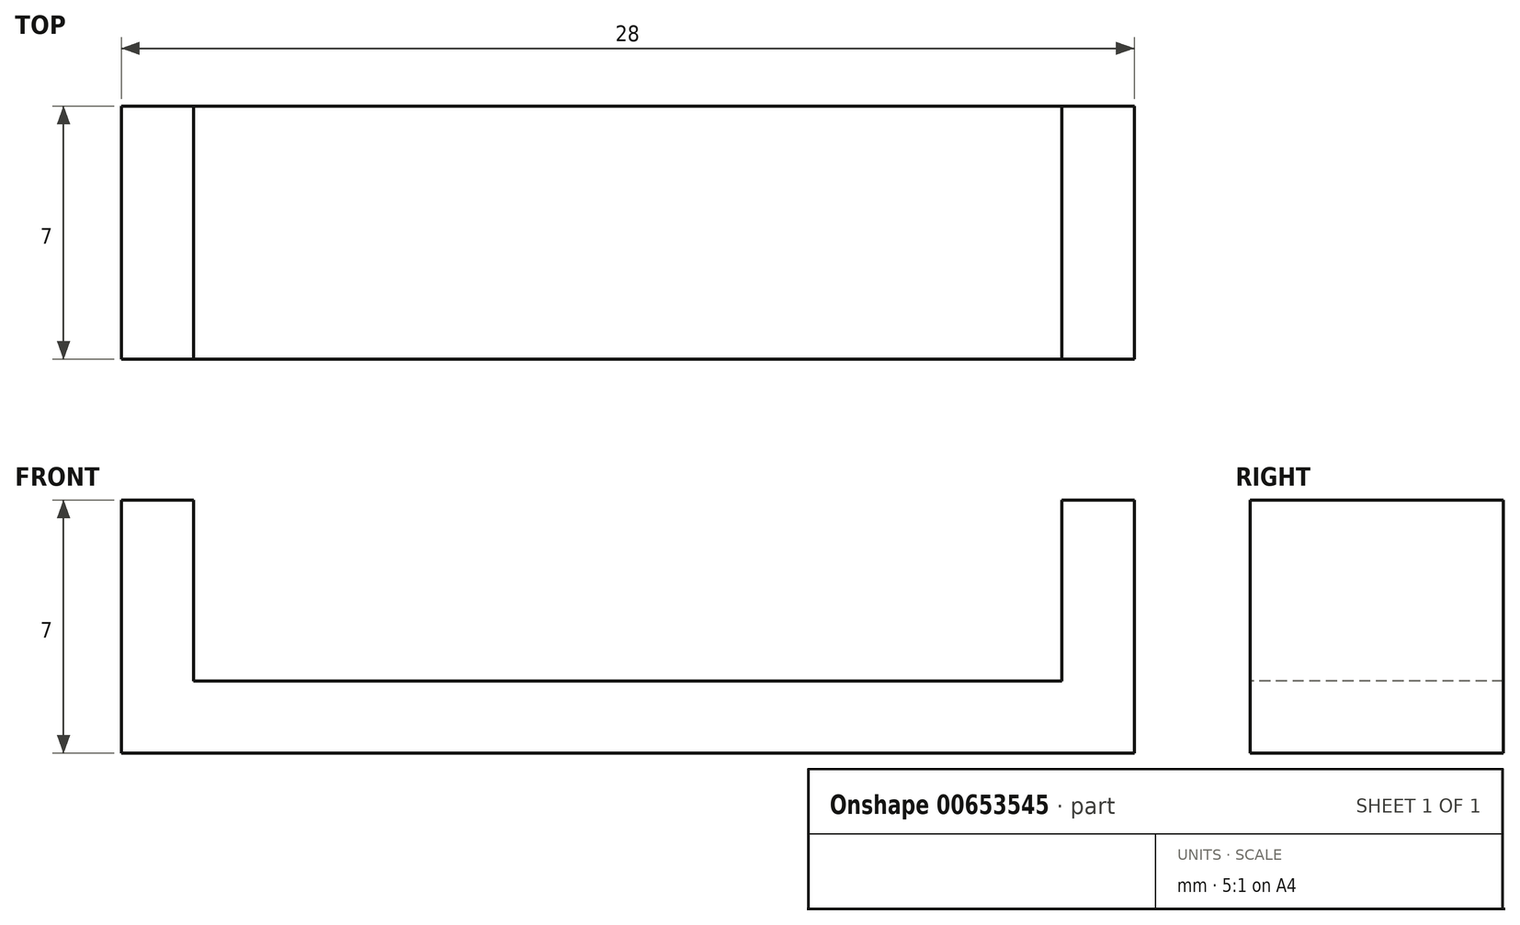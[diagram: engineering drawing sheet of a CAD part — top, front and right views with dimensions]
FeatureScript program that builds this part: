
annotation { "Feature Type Name" : "Feature", "Feature Type Description" : "" }
export const myFeature = defineFeature(function(context is Context, id is Id, definition is map)
    precondition{}
    {
        {
            var Q0;
            Q0=qCreatedBy(makeId("Front.planeOp"),FACE);
            var sketch = newSketch(context, id + "F0", { "sketchPlane" : qUnion([Q0])});
            skLineSegment(sketch, "E0", {"start": v(0, 0) * mm, "end": v(12, 0) * mm});
            skLineSegment(sketch, "E1", {"start": v(12, 0) * mm, "end": v(14, 0) * mm});
            skLineSegment(sketch, "E2", {"start": v(14, 0) * mm, "end": v(14, 7) * mm});
            skLineSegment(sketch, "E3", {"start": v(14, 7) * mm, "end": v(12, 7) * mm});
            skLineSegment(sketch, "E4", {"start": v(12, 7) * mm, "end": v(12, 0) * mm});
            skLineSegment(sketch, "E5", {"start": v(0, 0) * mm, "end": v(0, 2) * mm});
            skLineSegment(sketch, "E6", {"start": v(0, 2) * mm, "end": v(12, 2) * mm});
            skSolve(sketch);
        }
        {
            var Q0;
            Q0=makeQuery(id+"F0.imprint","IMPRINT",FACE,{"disambiguationData":[TD([[makeQuery(id+"F0.imprint","IMPRINT",EDGE,{"derivedFrom":sQuery(id+"F0.wireOp",EDGE,"E1")}),1.0]])]});
            var Q1;
            {var subQ0=sQuery(id+"F0.wireOp",EDGE,"E0");Q1=makeQuery(id+"F0.imprint","IMPRINT",FACE,{"disambiguationData":[TD([[makeQuery(id+"F0.imprint","IMPRINT",EDGE,{"derivedFrom":subQ0}),1.0]])]});}
            extrude(context, id + "F1", {"entities" : qUnion([Q0, Q1]), "oppositeDirection" : true, "depth" : 7 * mm, "offsetDistance" : 25 * mm});
        }
        {
            var Q0;
            Q0=makeQuery(id+"F1.opExtrude","SWEPT_BODY",BODY,{"disambiguationData":[OSD([sQuery(id+"F0.wireOp",EDGE,"E0"),sQuery(id+"F0.wireOp",EDGE,"E1"),sQuery(id+"F0.wireOp",EDGE,"E2"),sQuery(id+"F0.wireOp",EDGE,"E3"),sQuery(id+"F0.wireOp",EDGE,"E4"),sQuery(id+"F0.wireOp",EDGE,"E5"),sQuery(id+"F0.wireOp",EDGE,"E6")])]});
            var Q1;
            Q1=qCreatedBy(makeId("Right.planeOp"),FACE);
            mirror(context, id + "F2", {"operationType" : NewBodyOperationType.ADD, "entities" : qUnion([Q0]), "mirrorPlane" : qUnion([Q1])});
        }
    });
